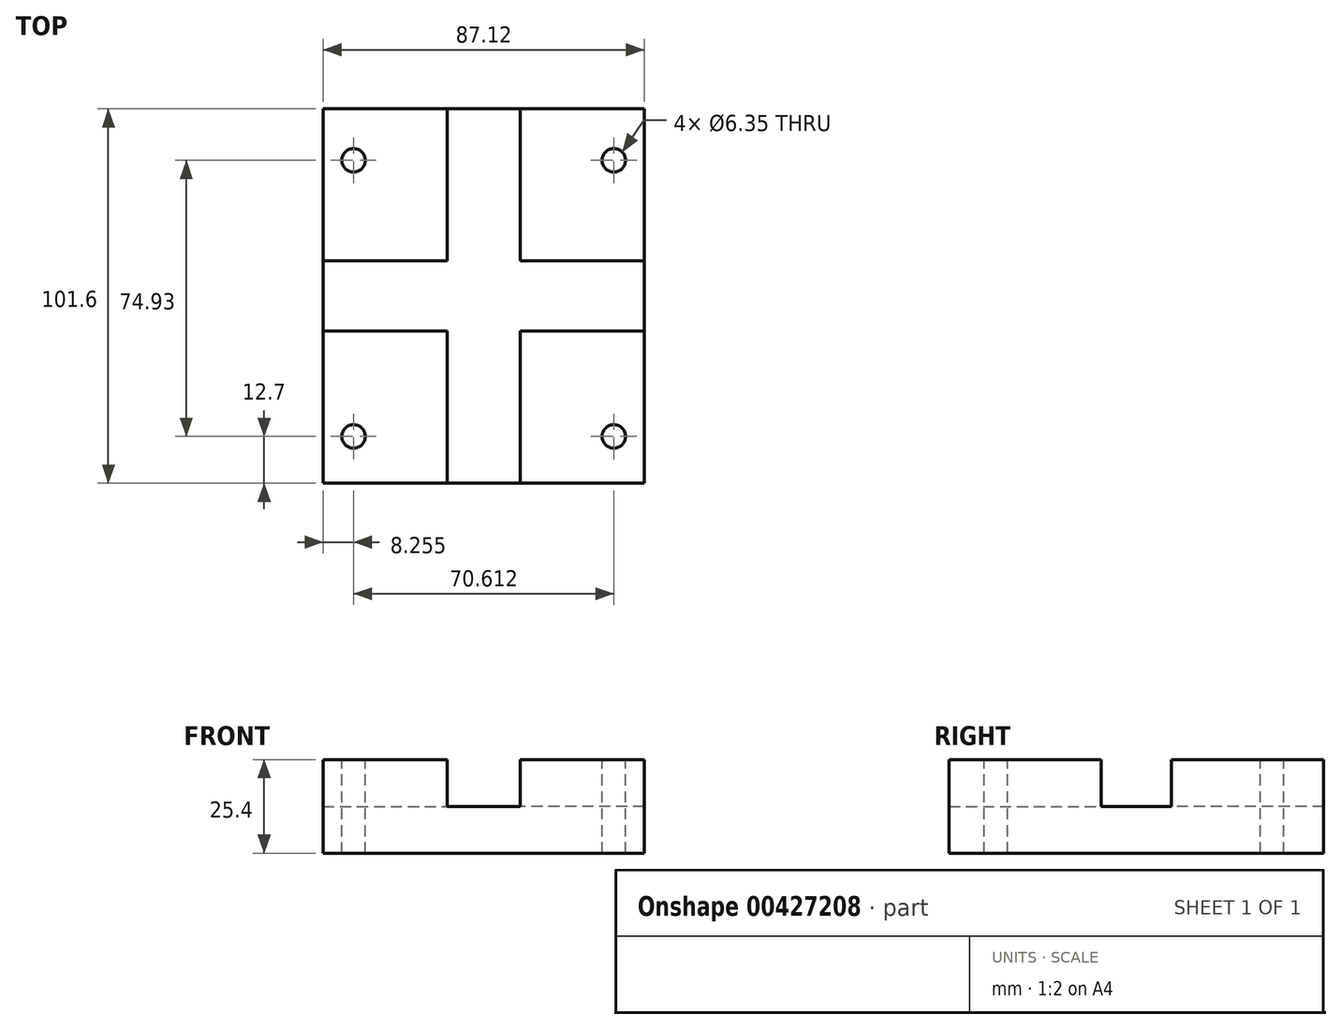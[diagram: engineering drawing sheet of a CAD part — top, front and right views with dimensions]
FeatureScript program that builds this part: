
annotation { "Feature Type Name" : "Feature", "Feature Type Description" : "" }
export const myFeature = defineFeature(function(context is Context, id is Id, definition is map)
    precondition{}
    {
        {
            var Q0;
            Q0=qCreatedBy(makeId("Top.planeOp"),FACE);
            var sketch = newSketch(context, id + "F0", { "sketchPlane" : qUnion([Q0])});
            skLineSegment(sketch, "E0.bottom", {"start": v(0, 0) * mm, "end": v(87.12, 0) * mm});
            skLineSegment(sketch, "E0.top", {"start": v(0, 101.6) * mm, "end": v(87.12, 101.6) * mm});
            skLineSegment(sketch, "E0.left", {"start": v(0, 0) * mm, "end": v(0, 101.6) * mm});
            skLineSegment(sketch, "E0.right", {"start": v(87.12, 0) * mm, "end": v(87.12, 101.6) * mm});
            skSolve(sketch);
        }
        {
            var Q0;
            Q0 = qSketchRegion(id + "F0", true);
            extrude(context, id + "F1", {"entities" : qUnion([Q0]), "depth" : 12.7 * mm});
        }
        {
            var Q0;
            Q0=makeQuery(id+"F1.opExtrude","CAP_FACE",FACE,{"disambiguationData":[OSD([sQuery(id+"F0.wireOp",EDGE,"E0.bottom"),sQuery(id+"F0.wireOp",EDGE,"E0.top"),sQuery(id+"F0.wireOp",EDGE,"E0.left"),sQuery(id+"F0.wireOp",EDGE,"E0.right")])],"isStart":false});
            var sketch = newSketch(context, id + "F2", { "sketchPlane" : qUnion([Q0])});
            skLineSegment(sketch, "E1.bottom", {"start": v(0, 101.6) * mm, "end": v(33.65, 101.6) * mm});
            skLineSegment(sketch, "E1.top", {"start": v(0, 60.32) * mm, "end": v(33.66, 60.32) * mm});
            skLineSegment(sketch, "E1.left", {"start": v(0, 101.6) * mm, "end": v(0, 60.32) * mm});
            skLineSegment(sketch, "E1.right", {"start": v(33.65, 101.6) * mm, "end": v(33.65, 60.32) * mm});
            skLineSegment(sketch, "E2.bottom", {"start": v(87.12, 101.6) * mm, "end": v(53.47, 101.6) * mm});
            skLineSegment(sketch, "E2.top", {"start": v(87.12, 60.33) * mm, "end": v(53.47, 60.33) * mm});
            skLineSegment(sketch, "E2.left", {"start": v(87.12, 101.6) * mm, "end": v(87.12, 60.33) * mm});
            skLineSegment(sketch, "E2.right", {"start": v(53.47, 101.6) * mm, "end": v(53.47, 60.33) * mm});
            skLineSegment(sketch, "E3.bottom", {"start": v(87.12, 0) * mm, "end": v(53.47, 0) * mm});
            skLineSegment(sketch, "E3.top", {"start": v(87.12, 41.28) * mm, "end": v(53.47, 41.28) * mm});
            skLineSegment(sketch, "E3.left", {"start": v(87.12, 0) * mm, "end": v(87.12, 41.28) * mm});
            skLineSegment(sketch, "E3.right", {"start": v(53.47, 0) * mm, "end": v(53.47, 41.28) * mm});
            skLineSegment(sketch, "E4.bottom", {"start": v(0, 0) * mm, "end": v(33.65, 0) * mm});
            skLineSegment(sketch, "E4.top", {"start": v(0, 41.27) * mm, "end": v(33.65, 41.27) * mm});
            skLineSegment(sketch, "E4.left", {"start": v(0, 0) * mm, "end": v(0, 41.27) * mm});
            skLineSegment(sketch, "E4.right", {"start": v(33.65, 0) * mm, "end": v(33.65, 41.27) * mm});
            skLineSegment(sketch, "E5.bottom", {"start": v(77.89, 41.28) * mm, "end": v(73.55, 41.28) * mm});
            skSolve(sketch);
        }
        {
            var Q0;
            Q0 = qSketchRegion(id + "F2", true);
            extrude(context, id + "F3", {"entities" : qUnion([Q0]), "operationType" : NewBodyOperationType.ADD, "depth" : 12.7 * mm});
        }
        {
            var Q0;
            Q0=makeQuery(id+"F3.opExtrude","CAP_FACE",FACE,{"disambiguationData":[OSD([sQuery(id+"F2.wireOp",EDGE,"E2.bottom"),sQuery(id+"F2.wireOp",EDGE,"E2.top"),sQuery(id+"F2.wireOp",EDGE,"E2.left"),sQuery(id+"F2.wireOp",EDGE,"E2.right")])],"isStart":false});
            var sketch = newSketch(context, id + "F4", { "sketchPlane" : qUnion([Q0])});
            skCircle(sketch, "E6", {"center": v(78.87, 87.63) * mm, "radius": 3.18 * mm});
            skCircle(sketch, "E7", {"center": v(8.26, 87.63) * mm, "radius": 3.18 * mm});
            skCircle(sketch, "E8", {"center": v(78.87, 12.7) * mm, "radius": 3.18 * mm});
            skCircle(sketch, "E9", {"center": v(8.26, 12.7) * mm, "radius": 3.18 * mm});
            skSolve(sketch);
        }
        {
            var Q0;
            Q0 = qSketchRegion(id + "F4", true);
            extrude(context, id + "F5", {"entities" : qUnion([Q0]), "operationType" : NewBodyOperationType.REMOVE, "oppositeDirection" : true, "depth" : 25.4 * mm});
        }
    });
